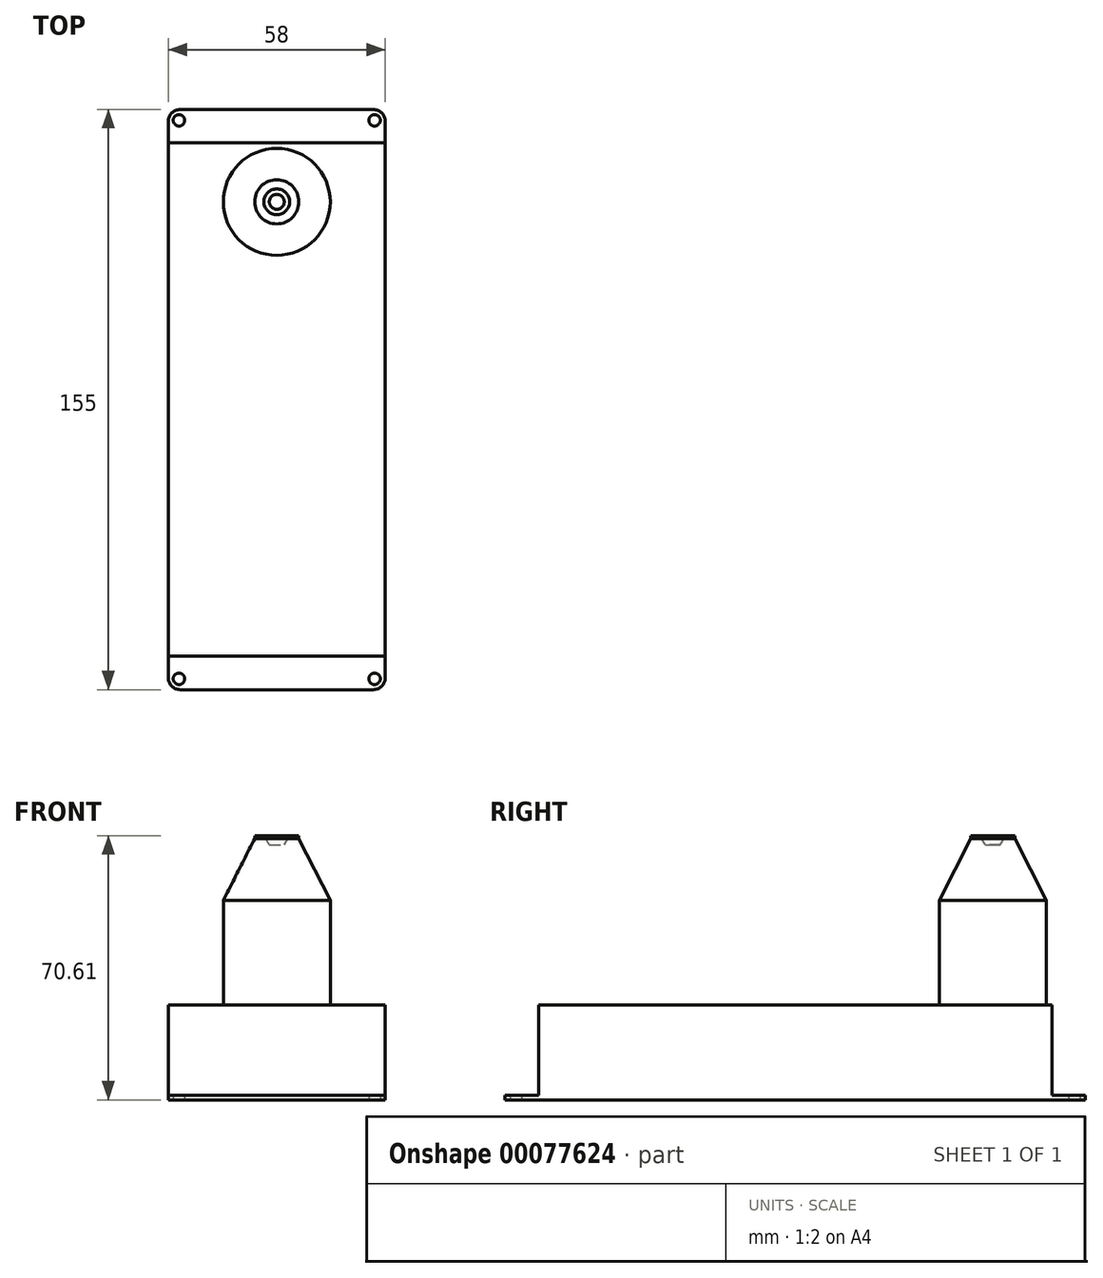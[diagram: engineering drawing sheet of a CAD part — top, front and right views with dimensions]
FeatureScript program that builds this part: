
annotation { "Feature Type Name" : "Feature", "Feature Type Description" : "" }
export const myFeature = defineFeature(function(context is Context, id is Id, definition is map)
    precondition{}
    {
        {
            var Q0;
            Q0=qCreatedBy(makeId("Top.planeOp"),FACE);
            var sketch = newSketch(context, id + "F0", { "sketchPlane" : qUnion([Q0])});
            skLineSegment(sketch, "E0.bottom", {"start": v(25.83, -130.34) * mm, "end": v(-25.82, -130.34) * mm});
            skLineSegment(sketch, "E0.top", {"start": v(25.83, 24.66) * mm, "end": v(-25.83, 24.66) * mm});
            skLineSegment(sketch, "E0.left", {"start": v(29, -127.17) * mm, "end": v(29, 21.48) * mm});
            skLineSegment(sketch, "E0.right", {"start": v(-29, -127.17) * mm, "end": v(-29, 21.48) * mm});
            skLineSegment(sketch, "E1", {"start": v(0, 24.66) * mm, "end": v(0, -130.34) * mm, "construction": true});
            skLineSegment(sketch, "E2", {"start": v(-29, -52.84) * mm, "end": v(29, -52.84) * mm, "construction": true});
            skCircle(sketch, "E3", {"center": v(-26.14, 21.77) * mm, "radius": 1.52 * mm});
            skCircle(sketch, "E4.MirrorC", {"center": v(26.14, 21.77) * mm, "radius": 1.52 * mm});
            skCircle(sketch, "E5.MirrorC", {"center": v(-26.14, -127.46) * mm, "radius": 1.52 * mm});
            skCircle(sketch, "E6.MirrorC", {"center": v(26.14, -127.46) * mm, "radius": 1.52 * mm});
            skPoint(sketch, "E7.visualSharp", {"position": v(-29, 24.66) * mm});
            skArc(sketch, "E7.filletArc", {"start": v(-25.83, 24.66) * mm, "mid": v(-28.07, 23.73) * mm, "end": v(-29, 21.48) * mm});
            skPoint(sketch, "E8.visualSharp", {"position": v(29, 24.66) * mm});
            skArc(sketch, "E8.filletArc", {"start": v(29, 21.48) * mm, "mid": v(28.07, 23.73) * mm, "end": v(25.83, 24.66) * mm});
            skArc(sketch, "E9.filletArc", {"start": v(25.83, -130.34) * mm, "mid": v(28.07, -129.41) * mm, "end": v(29, -127.17) * mm});
            skPoint(sketch, "E10.visualSharp", {"position": v(-29, -130.34) * mm});
            skArc(sketch, "E10.filletArc", {"start": v(-29, -127.17) * mm, "mid": v(-28.07, -129.41) * mm, "end": v(-25.82, -130.34) * mm});
            skPoint(sketch, "E11", {"position": v(0, -52.84) * mm});
            skPoint(sketch, "E12", {"position": v(0, 0) * mm});
            skLineSegment(sketch, "E13.bottom", {"start": v(29, -121.42) * mm, "end": v(-29, -121.42) * mm});
            skLineSegment(sketch, "E13.top", {"start": v(29, 15.74) * mm, "end": v(-29, 15.74) * mm});
            skLineSegment(sketch, "E13.left", {"start": v(29, -121.42) * mm, "end": v(29, 15.74) * mm});
            skLineSegment(sketch, "E13.right", {"start": v(-29, -121.42) * mm, "end": v(-29, 15.74) * mm});
            skSolve(sketch);
        }
        {
            var Q0;
            Q0=makeQuery(id+"F0.imprint","IMPRINT",FACE,{"disambiguationData":[TD([[makeQuery(id+"F0.imprint","IMPRINT",EDGE,{"derivedFrom":sQuery(id+"F0.wireOp",EDGE,"E13.bottom")}),-1.0]])]});
            var Q1;
            Q1=makeQuery(id+"F0.imprint","IMPRINT",FACE,{"disambiguationData":[TD([[makeQuery(id+"F0.imprint","IMPRINT",EDGE,{"derivedFrom":sQuery(id+"F0.wireOp",EDGE,"E0.top")}),1.0]])]});
            var Q2;
            Q2=makeQuery(id+"F0.imprint","IMPRINT",FACE,{"disambiguationData":[TD([[makeQuery(id+"F0.imprint","IMPRINT",EDGE,{"derivedFrom":sQuery(id+"F0.wireOp",EDGE,"E0.bottom")}),-1.0]])]});
            extrude(context, id + "F1", {"entities" : qUnion([Q0, Q1, Q2]), "depth" : 1.27 * mm});
        }
        {
            var Q0;
            Q0=makeQuery(id+"F0.imprint","IMPRINT",FACE,{"disambiguationData":[TD([[makeQuery(id+"F0.imprint","IMPRINT",EDGE,{"derivedFrom":sQuery(id+"F0.wireOp",EDGE,"E13.bottom")}),-1.0]])]});
            var Q1;
            Q1=makeQuery(id+"F1.opExtrude","CAP_FACE",FACE,{"disambiguationData":[OSD([sQuery(id+"F0.wireOp",EDGE,"E0.bottom"),sQuery(id+"F0.wireOp",EDGE,"E0.top"),sQuery(id+"F0.wireOp",EDGE,"E0.left"),sQuery(id+"F0.wireOp",EDGE,"E0.right"),sQuery(id+"F0.wireOp",EDGE,"E3"),sQuery(id+"F0.wireOp",EDGE,"E4.MirrorC"),sQuery(id+"F0.wireOp",EDGE,"E5.MirrorC"),sQuery(id+"F0.wireOp",EDGE,"E6.MirrorC"),sQuery(id+"F0.wireOp",EDGE,"E7.filletArc"),sQuery(id+"F0.wireOp",EDGE,"E8.filletArc"),sQuery(id+"F0.wireOp",EDGE,"E9.filletArc"),sQuery(id+"F0.wireOp",EDGE,"E10.filletArc"),sQuery(id+"F0.wireOp",EDGE,"E13.left"),sQuery(id+"F0.wireOp",EDGE,"E13.right")])],"isStart":false});
            extrude(context, id + "F2", {"entities" : qUnion([Q0]), "operationType" : NewBodyOperationType.ADD, "depth" : 25.4 * mm, "hasSecondDirection" : true, "secondDirectionBound" : SecondDirectionBoundingType.UP_TO_SURFACE, "secondDirectionOppositeDirection" : false, "secondDirectionBoundEntityFace" : qUnion([Q1]), "secondDirectionDepth" : 25.4 * mm});
        }
        {
            var Q0;
            Q0=qCreatedBy(makeId("Right.planeOp"),FACE);
            var sketch = newSketch(context, id + "F3", { "sketchPlane" : qUnion([Q0])});
            skLineSegment(sketch, "E14", {"start": v(3.45, 70.61) * mm, "end": v(5.9, 70.61) * mm});
            skLineSegment(sketch, "E15", {"start": v(5.9, 70.61) * mm, "end": v(5.9, 69.85) * mm});
            skLineSegment(sketch, "E16", {"start": v(5.9, 69.85) * mm, "end": v(14.29, 53.26) * mm});
            skLineSegment(sketch, "E17", {"start": v(14.29, 53.26) * mm, "end": v(14.29, 25.4) * mm});
            skLineSegment(sketch, "E18.0.0", {"start": v(-127.17, 0) * mm, "end": v(21.48, 0) * mm});
            skLineSegment(sketch, "E18.0.1", {"start": v(21.48, 0) * mm, "end": v(21.48, 1.27) * mm});
            skLineSegment(sketch, "E18.0.2", {"start": v(21.48, 1.27) * mm, "end": v(15.74, 1.27) * mm});
            skLineSegment(sketch, "E18.0.3", {"start": v(15.74, 1.27) * mm, "end": v(15.74, 25.4) * mm});
            skLineSegment(sketch, "E18.0.4", {"start": v(15.74, 25.4) * mm, "end": v(-121.42, 25.4) * mm});
            skLineSegment(sketch, "E18.0.5", {"start": v(-121.42, 25.4) * mm, "end": v(-121.42, 1.27) * mm});
            skLineSegment(sketch, "E18.0.6", {"start": v(-121.42, 1.27) * mm, "end": v(-127.17, 1.27) * mm});
            skLineSegment(sketch, "E18.0.7", {"start": v(-127.17, 1.27) * mm, "end": v(-127.17, 0) * mm});
            skLineSegment(sketch, "E19", {"start": v(0, 0) * mm, "end": v(0, 87.43) * mm, "construction": true});
            skLineSegment(sketch, "E20", {"start": v(0, 68.2) * mm, "end": v(2, 68.2) * mm});
            skLineSegment(sketch, "E21", {"start": v(0, 68.2) * mm, "end": v(19.17, 81.62) * mm, "construction": true});
            skLineSegment(sketch, "E22", {"start": v(2, 68.2) * mm, "end": v(3.45, 70.61) * mm});
            skPoint(sketch, "E23.orphan", {"position": v(0, 70.61) * mm});
            skLineSegment(sketch, "E24", {"start": v(14.29, 25.4) * mm, "end": v(0, 25.4) * mm});
            skLineSegment(sketch, "E25", {"start": v(0, 25.4) * mm, "end": v(0, 68.2) * mm});
            skSolve(sketch);
        }
        {
            var Q0;
            Q0=makeQuery(id+"F3.imprint","IMPRINT",FACE,{"disambiguationData":[TD([[makeQuery(id+"F3.imprint","IMPRINT",EDGE,{"derivedFrom":sQuery(id+"F3.wireOp",EDGE,"E14")}),-1.0]])]});
            var Q1;
            Q1=sQuery(id+"F3.wireOp",EDGE,"E19");
            revolve(context, id + "F4", {"operationType" : NewBodyOperationType.ADD, "entities" : qUnion([Q0]), "axis" : qUnion([Q1]), "revolveType" : RevolveType.FULL});
        }
    });
